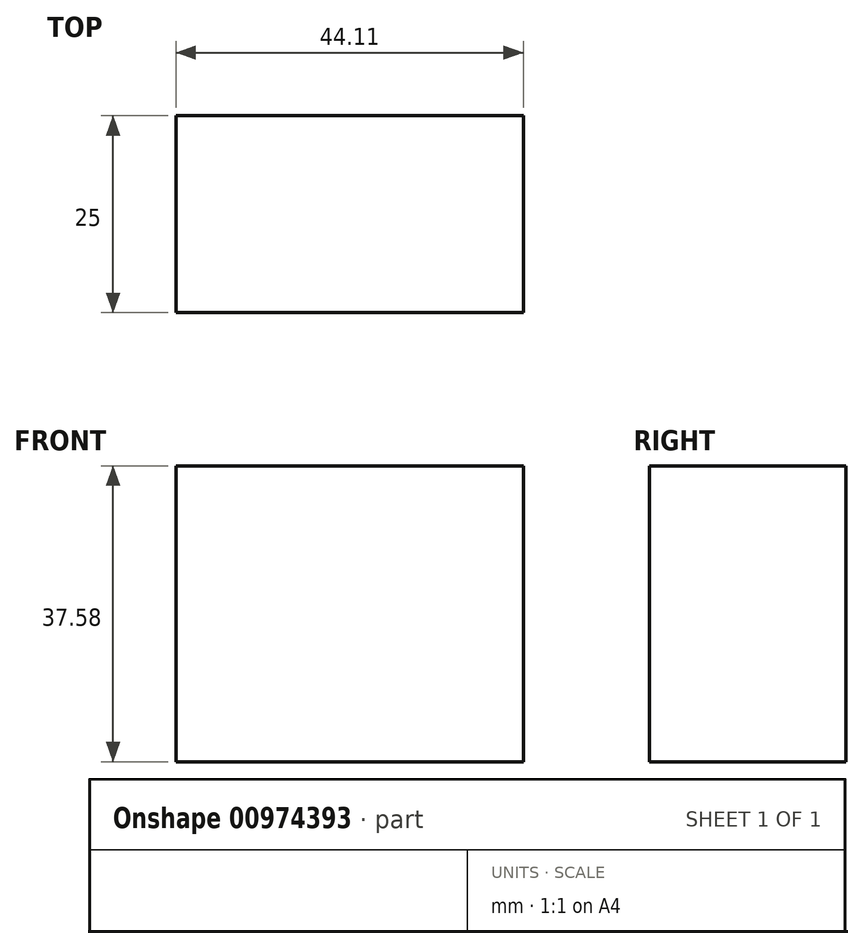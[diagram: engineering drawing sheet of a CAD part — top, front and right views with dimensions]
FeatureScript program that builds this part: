
annotation { "Feature Type Name" : "Feature", "Feature Type Description" : "" }
export const myFeature = defineFeature(function(context is Context, id is Id, definition is map)
    precondition{}
    {
        {
            var Q0;
            Q0=qCreatedBy(makeId("Front.planeOp"),FACE);
            var sketch = newSketch(context, id + "F0", { "sketchPlane" : qUnion([Q0])});
            skLineSegment(sketch, "E0.bottom", {"start": v(-70.99, 30.96) * mm, "end": v(-26.88, 30.96) * mm});
            skLineSegment(sketch, "E0.top", {"start": v(-70.99, -6.62) * mm, "end": v(-26.88, -6.62) * mm});
            skLineSegment(sketch, "E0.left", {"start": v(-70.99, 30.96) * mm, "end": v(-70.99, -6.62) * mm});
            skLineSegment(sketch, "E0.right", {"start": v(-26.88, 30.96) * mm, "end": v(-26.88, -6.62) * mm});
            skSolve(sketch);
        }
        {
            var Q0;
            Q0 = qSketchRegion(id + "F0", true);
            extrude(context, id + "F1", {"entities" : qUnion([Q0]), "depth" : 25 * mm, "offsetDistance" : 25 * mm});
        }
    });
